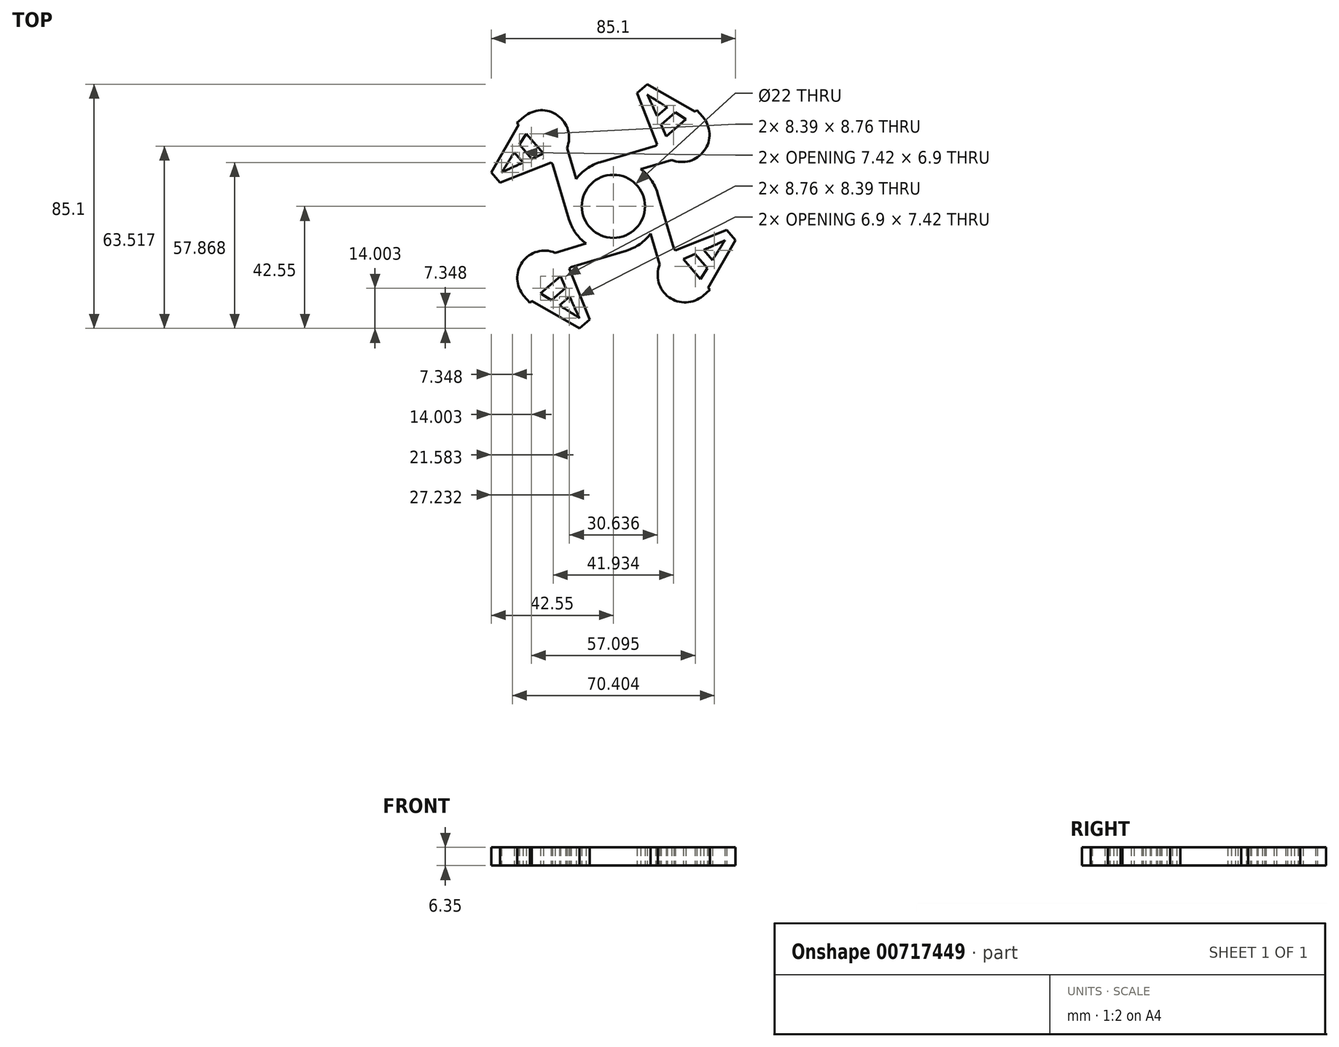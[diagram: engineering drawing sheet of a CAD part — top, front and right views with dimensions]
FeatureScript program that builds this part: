
annotation { "Feature Type Name" : "Feature", "Feature Type Description" : "" }
export const myFeature = defineFeature(function(context is Context, id is Id, definition is map)
    precondition{}
    {
        {
            var Q0;
            Q0=qCreatedBy(makeId("Top.planeOp"),FACE);
            var sketch = newSketch(context, id + "F0", { "sketchPlane" : qUnion([Q0])});
            skCircle(sketch, "E0", {"center": v(0, 0) * mm, "radius": 11 * mm});
            skCircle(sketch, "E1.cCircle", {"center": v(0, 0) * mm, "radius": 44.45 * mm, "construction": true});
            skLineSegment(sketch, "E1.0", {"start": v(31.43, -31.43) * mm, "end": v(-31.43, -31.43) * mm, "construction": true});
            skLineSegment(sketch, "E1.2", {"start": v(-31.43, 31.43) * mm, "end": v(31.43, 31.43) * mm, "construction": true});
            skLineSegment(sketch, "E1.3", {"start": v(31.43, 31.43) * mm, "end": v(31.43, -31.43) * mm, "construction": true});
            skLineSegment(sketch, "E2", {"start": v(29.1, 33.6) * mm, "end": v(31.17, 31.2) * mm});
            skLineSegment(sketch, "E3", {"start": v(30.2, 17.77) * mm, "end": v(30.2, 17.77) * mm});
            skLineSegment(sketch, "E4", {"start": v(16.77, 18.73) * mm, "end": v(14.7, 21.13) * mm});
            skLineSegment(sketch, "E5", {"start": v(14.7, 21.13) * mm, "end": v(29.1, 33.6) * mm});
            skPoint(sketch, "E6.visualSharp", {"position": v(37.4, 24) * mm});
            skArc(sketch, "E6.filletArc", {"start": v(30.2, 17.77) * mm, "mid": v(33.47, 24.29) * mm, "end": v(31.17, 31.2) * mm});
            skArc(sketch, "E7.filletArc", {"start": v(16.77, 18.73) * mm, "mid": v(23.3, 15.47) * mm, "end": v(30.2, 17.77) * mm});
            skLineSegment(sketch, "E8", {"start": v(23.97, 24.97) * mm, "end": v(31.43, 31.43) * mm, "construction": true});
            skCircle(sketch, "E9", {"center": v(0, 0) * mm, "radius": 16.08 * mm});
            skLineSegment(sketch, "E10", {"start": v(0, 0) * mm, "end": v(0, 31.43) * mm, "construction": true});
            skLineSegment(sketch, "E11", {"start": v(-4.57, 15.42) * mm, "end": v(14.7, 21.13) * mm});
            skLineSegment(sketch, "E12", {"start": v(20.31, 16.18) * mm, "end": v(9.5, 12.97) * mm});
            skArc(sketch, "E13.1.0", {"start": v(-18.73, 16.77) * mm, "mid": v(-15.47, 23.3) * mm, "end": v(-17.77, 30.2) * mm});
            skLineSegment(sketch, "E13.1.1", {"start": v(-16.18, 20.31) * mm, "end": v(-12.97, 9.5) * mm});
            skLineSegment(sketch, "E13.1.2", {"start": v(-15.42, -4.57) * mm, "end": v(-21.13, 14.7) * mm});
            skLineSegment(sketch, "E13.1.3", {"start": v(-21.13, 14.7) * mm, "end": v(-33.6, 29.1) * mm});
            skLineSegment(sketch, "E13.1.4", {"start": v(-33.6, 29.1) * mm, "end": v(-31.2, 31.17) * mm});
            skArc(sketch, "E13.1.5", {"start": v(-17.77, 30.2) * mm, "mid": v(-24.29, 33.47) * mm, "end": v(-31.2, 31.17) * mm});
            skLineSegment(sketch, "E13.1.6", {"start": v(-18.73, 16.77) * mm, "end": v(-21.13, 14.7) * mm});
            skArc(sketch, "E13.2.0", {"start": v(-16.77, -18.73) * mm, "mid": v(-23.3, -15.47) * mm, "end": v(-30.2, -17.77) * mm});
            skLineSegment(sketch, "E13.2.1", {"start": v(-20.31, -16.18) * mm, "end": v(-9.5, -12.97) * mm});
            skLineSegment(sketch, "E13.2.2", {"start": v(4.57, -15.42) * mm, "end": v(-14.7, -21.13) * mm});
            skLineSegment(sketch, "E13.2.3", {"start": v(-14.7, -21.13) * mm, "end": v(-29.1, -33.6) * mm});
            skLineSegment(sketch, "E13.2.4", {"start": v(-29.1, -33.6) * mm, "end": v(-31.17, -31.2) * mm});
            skArc(sketch, "E13.2.5", {"start": v(-30.2, -17.77) * mm, "mid": v(-33.47, -24.29) * mm, "end": v(-31.17, -31.2) * mm});
            skLineSegment(sketch, "E13.2.6", {"start": v(-16.77, -18.73) * mm, "end": v(-14.7, -21.13) * mm});
            skArc(sketch, "E13.3.0", {"start": v(18.73, -16.77) * mm, "mid": v(15.47, -23.3) * mm, "end": v(17.77, -30.2) * mm});
            skLineSegment(sketch, "E13.3.1", {"start": v(16.18, -20.31) * mm, "end": v(12.97, -9.5) * mm});
            skLineSegment(sketch, "E13.3.2", {"start": v(15.42, 4.57) * mm, "end": v(21.13, -14.7) * mm});
            skLineSegment(sketch, "E13.3.3", {"start": v(21.13, -14.7) * mm, "end": v(33.6, -29.1) * mm});
            skLineSegment(sketch, "E13.3.4", {"start": v(33.6, -29.1) * mm, "end": v(31.2, -31.17) * mm});
            skArc(sketch, "E13.3.5", {"start": v(17.77, -30.2) * mm, "mid": v(24.29, -33.47) * mm, "end": v(31.2, -31.17) * mm});
            skLineSegment(sketch, "E13.3.6", {"start": v(18.73, -16.77) * mm, "end": v(21.13, -14.7) * mm});
            skText(sketch, "E14", { "text": "A", "fontName": "OpenSans-Bold.ttf"});
            skText(sketch, "E15", { "text": "A", "fontName": "OpenSans-Bold.ttf"});
            skText(sketch, "E16", { "text": "A", "fontName": "OpenSans-Bold.ttf"});
            skText(sketch, "E17", { "text": "A", "fontName": "OpenSans-Bold.ttf"});
            skLineSegment(sketch, "E18", {"start": v(-31.43, 31.43) * mm, "end": v(-31.43, -31.43) * mm, "construction": true});
            const initialGuessF0  = {"E14": [0.0153, 0.02165, 0.7558, 0.6548, 0.01817], "E15": [0.02165, -0.0153, 0.6548, -0.7558, 0.01817], "E16": [-0.0153, -0.02165, -0.7558, -0.6548, 0.01817], "E17": [-0.02165, 0.0153, -0.6548, 0.7558, 0.01817]};
            skSetInitialGuess(sketch, initialGuessF0);
            skSolve(sketch);
        }
        {
            var Q0;
            Q0=qSketchRegion(id+"F0",true);
            extrude(context, id + "F1", {"entities" : qUnion([Q0]), "depth" : 6.35 * mm, "offsetDistance" : 25.4 * mm});
        }
    });
